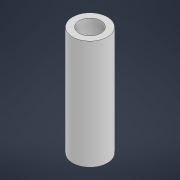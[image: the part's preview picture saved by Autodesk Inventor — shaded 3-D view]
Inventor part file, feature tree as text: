
AUTODESK INVENTOR PART (.ipt)
format: ipt  version: 2021 (Build 250183000, 183)  size: 88,064 bytes
history: native  units: mm
features: extrude x1, sketch x1
ambient origin geometry x8: Origin, YZ Plane, XZ Plane, XY Plane, X Axis, Y Axis, Z Axis, Center Point
bodies: Volumenkörper1 (feature_tree)
feature tree (2):
  extrude  "Extrusion1"  Depth=22.0mm
  sketch  "Skizze1"  dims[d0=7.0mm d1=4.4mm d2=22.0mm d3=0.0mm]
